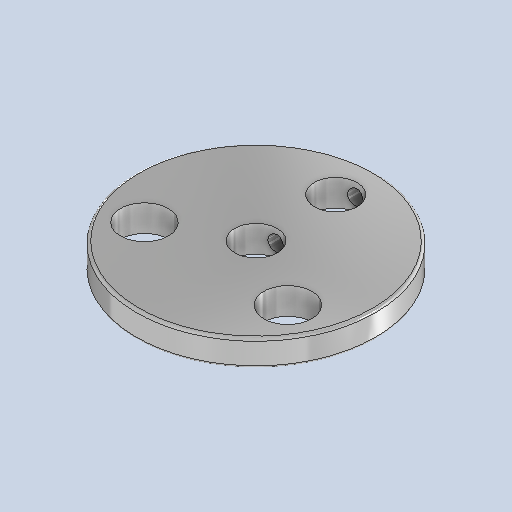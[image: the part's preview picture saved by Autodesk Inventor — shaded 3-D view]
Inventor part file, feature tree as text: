
AUTODESK INVENTOR PART (.ipt)
format: ipt  version: 2025.1 (Build 291241000, 241)  size: 285,184 bytes
history: native  units: mm
features: sketch x3, extrude x2, projected_geometry x2, fillet x1, plane x1, hole x1
ambient origin geometry x8: Origin, YZ Plane, XZ Plane, XY Plane, X Axis, Y Axis, Z Axis, Center Point
bodies: Solid1 (feature_tree)
feature tree (10):
  extrude  "Extrusion1"  Depth=5.0mm TaperAngle=0.0deg
  extrude  "Extrusion2"  Depth=15.0mm
  fillet  "Fillet1"  Radius=8.0mm
  plane  "Work Plane1"
  hole  "Hole1"  [1 undecoded]
  sketch  "Sketch1"  dims[d0=45.0mm d1=5.0mm d2=0.0mm]
  sketch  "Sketch2"  dims[d3=8.0mm d4=15.0mm d5=8.0mm]
  sketch  "Sketch3"  dims[d6=7.5mm d7=13.5mm d8=13.5mm d9=9.0mm d10=9.0mm d11=9.0mm d12=0.0mm d13=0.5mm d14=3.0mm d15=3.0mm d16=6.0mm d17=4.0mm d18=2.0mm d19=90.0deg d20=8.0mm d21=20.594885mm]
  projected_geometry  "Projected Loop1"
  projected_geometry  "Projected Loop2"
note: 1 required parameter value undecoded (feature->parameter linkage not recoverable at this tier; creation-order binding heuristic only, values carry confidence <= 0.55)
